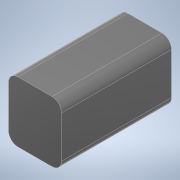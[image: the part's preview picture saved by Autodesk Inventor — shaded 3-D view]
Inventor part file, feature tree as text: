
AUTODESK INVENTOR PART (.ipt)
format: ipt  version: 2022.2 (Build 262287010, 287A)  size: 103,936 bytes
history: native  units: mm
features: other x1, extrude x1, fillet x1, sketch x1
ambient origin geometry x8: Origin, YZ Plane, XZ Plane, XY Plane, X Axis, Y Axis, Z Axis, Center Point
bodies: Body1 (feature_tree)
feature tree (4):
  other  "ソリッド1"
  extrude  "押し出し1"  Depth=28.0mm
  fillet  "フィレット1"  Radius=32.0mm
  sketch  "スケッチ1"
